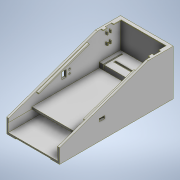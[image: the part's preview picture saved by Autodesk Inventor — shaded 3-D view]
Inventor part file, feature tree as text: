
AUTODESK INVENTOR PART (.ipt)
format: ipt  version: 2021 (Build 250183000, 183)  size: 753,664 bytes
history: native  units: mm
features: extrude x34, sketch x34, hole x1, projected_geometry x1, other x1
ambient origin geometry x8: Origin, YZ Plane, XZ Plane, XY Plane, X Axis, Y Axis, Z Axis, Center Point
bodies: 实体1 (feature_tree)
feature tree (71):
  extrude  "拉伸1"  Depth=80.0mm
  extrude  "拉伸2"  Depth=3.0mm
  extrude  "拉伸3"  Depth=2.5mm
  extrude  "拉伸4"  Depth=170.0mm TaperAngle=0.0deg
  extrude  "拉伸5"  Depth=3.0mm
  extrude  "拉伸8"  Depth=13.75mm
  extrude  "拉伸9"  Depth=45.0mm TaperAngle=0.0deg
  extrude  "拉伸10"  Depth=22.0mm
  extrude  "拉伸11"  Depth=3.0mm
  extrude  "拉伸12"  Depth=48.0mm TaperAngle=0.0deg
  extrude  "拉伸13"  Depth=3.0mm
  extrude  "拉伸14"  Depth=32.0mm TaperAngle=0.0deg
  extrude  "拉伸15"  TaperAngle=0.0deg  [1 undecoded]
  extrude  "拉伸16"  Depth=4.5mm
  extrude  "拉伸20"  Depth=4.5mm
  extrude  "拉伸21"  Depth=0.75mm
  extrude  "拉伸22"  Depth=19.0mm
  extrude  "拉伸23"  Depth=1.0mm
  hole  "孔1"  [1 undecoded]
  extrude  "拉伸24"  Depth=3.0mm TaperAngle=0.0deg
  extrude  "拉伸25"  Depth=8.0mm
  extrude  "拉伸26"  Depth=5.0mm
  extrude  "拉伸29"  Depth=5.0mm
  extrude  "拉伸30"  Depth=5.0mm TaperAngle=0.0deg
  extrude  "拉伸31"  Depth=1.0mm
  extrude  "拉伸32"  Depth=2.0mm
  extrude  "拉伸33"  Depth=1.0mm
  extrude  "拉伸34"  Depth=3.0mm
  extrude  "拉伸35"  Depth=2.0mm TaperAngle=0.0deg
  extrude  "拉伸36"  Depth=13.5mm
  extrude  "拉伸38"  Depth=10.0mm
  extrude  "拉伸39"  Depth=8.0mm
  extrude  "拉伸40"  Depth=6.0mm
  extrude  "拉伸41"  Depth=6.0mm
  extrude  "拉伸42"  Depth=6.5mm
  sketch  "草图1"  dims[d0=172.0mm d1=80.0mm]
  sketch  "草图2"  dims[d2=70.0mm d3=0.0mm d4=3.0mm]
  sketch  "草图3"  dims[d5=2.5mm d6=2.5mm]
  sketch  "草图4"  dims[d7=13.5mm d8=170.0mm d9=0.0mm]
  sketch  "草图5"  dims[d10=52.5mm d11=3.0mm]
  sketch  "草图9"  dims[d12=21.0mm d13=13.75mm]
  sketch  "草图12"  dims[d14=80.0mm d15=45.0mm d16=0.0mm]
  sketch  "草图15"  dims[d17=35.0mm d18=22.0mm]
  sketch  "草图16"  dims[d19=80.0mm d20=0.0mm d21=3.0mm]
  sketch  "草图17"  dims[d22=3.0mm d23=48.0mm d24=0.0mm]
  sketch  "草图18"  dims[d34=3.0mm d35=3.0mm]
  sketch  "草图19"  dims[d36=3.0mm d38=32.0mm d39=0.0mm]
  sketch  "草图21"  dims[d40=0.0mm d41=0.0mm]
  sketch  "草图29"  dims[d42=3.0mm d43=0.0mm d44=4.5mm]
  sketch  "草图30"  dims[d45=3.0mm d46=0.0mm d47=4.5mm]
  sketch  "草图31"  dims[d48=3.0mm d49=0.0mm d50=0.75mm]
  sketch  "草图36"  dims[d51=4.5mm d52=19.0mm]
  sketch  "草图37"  dims[d53=3.0mm d54=0.0mm d55=1.0mm]
  sketch  "草图41"  dims[d56=3.0mm d57=0.0mm d58=2.25mm]
  sketch  "草图42"  dims[d59=2.0mm d60=3.0mm d61=0.0mm]
  sketch  "草图43"  dims[d62=4.0mm d63=8.0mm]
  projected_geometry  "投影回路1"
  sketch  "草图48"  dims[d65=3.0mm d66=0.0mm]
  sketch  "草图52"  dims[d80=71.0mm d81=0.0mm d82=71.0mm d83=0.0mm d84=71.0mm d85=0.0mm d86=71.0mm d87=0.0mm d88=71.0mm d89=0.0mm d90=71.0mm d91=0.0mm d92=71.0mm d93=0.0mm d94=5.0mm]
  sketch  "草图53"  dims[d95=1.75mm d96=5.0mm]
  sketch  "草图54"  dims[d97=10.5mm d98=5.0mm d99=0.0mm]
  sketch  "草图55"  dims[d139=3.0mm d140=65.0mm d141=0.0mm d142=0.0mm d144=1.0mm]
  sketch  "草图56"  dims[d145=2.0mm d146=100.0mm]
  sketch  "草图57"  dims[d147=2.0mm d148=1.0mm]
  sketch  "草图58"  dims[d149=74.0mm d150=0.0mm d151=3.0mm]
  sketch  "草图61"  dims[d152=3.0mm d153=2.0mm d154=0.0mm]
  sketch  "草图62"  dims[d159=80.0mm d160=13.5mm]
  sketch  "草图67"  dims[d161=13.5mm d162=10.0mm]
  sketch  "草图68"  dims[d163=1.0mm d164=0.0mm d165=8.0mm]
  sketch  "草图69"  dims[d166=8.0mm d167=6.0mm d168=6.0mm d169=2.013mm d170=1.0mm d171=4.0mm d172=2.0mm d173=90.0deg d174=1.0mm d175=20.594885mm d181=6.5mm d182=10.0mm d184=3.0mm d185=6.0mm d186=10.0mm d187=0.0mm d188=80.0mm d189=10.0mm d190=0.0mm d191=4.0mm d192=0.0mm d208=17.0mm d209=10.7mm d210=4.0mm d211=17.0mm d212=3.0mm d213=0.0mm d225=75.0mm d226=40.0mm d227=50.0mm d228=0.0mm d235=1.0mm d236=0.0mm d237=3.0mm d239=32.0mm d240=0.0mm d241=3.0mm d242=5.0mm d243=3.0mm d244=0.0mm d245=20.0mm d246=3.0mm d247=0.0mm d248=4.0mm d249=3.0mm d250=3.0mm d251=0.0mm d252=1.0mm d253=29.0mm d254=0.0mm d255=10.0mm d256=2.0mm d257=0.0mm d258=45.0mm d272=1.0mm d273=0.0mm d280=10.0mm d281=0.0mm d282=8.0mm d283=4.0mm d284=4.0mm d285=25.0mm d286=10.0mm d287=0.0mm d292=3.0mm d293=102.0mm d294=0.0mm d295=1.0mm d296=0.0mm d297=1.0mm d298=0.0mm d338=4.440689mm d339=6.776036mm d340=4.5mm]
  other  "线性尺寸 14"
note: 2 required parameter values undecoded (feature->parameter linkage not recoverable at this tier; creation-order binding heuristic only, values carry confidence <= 0.55)
